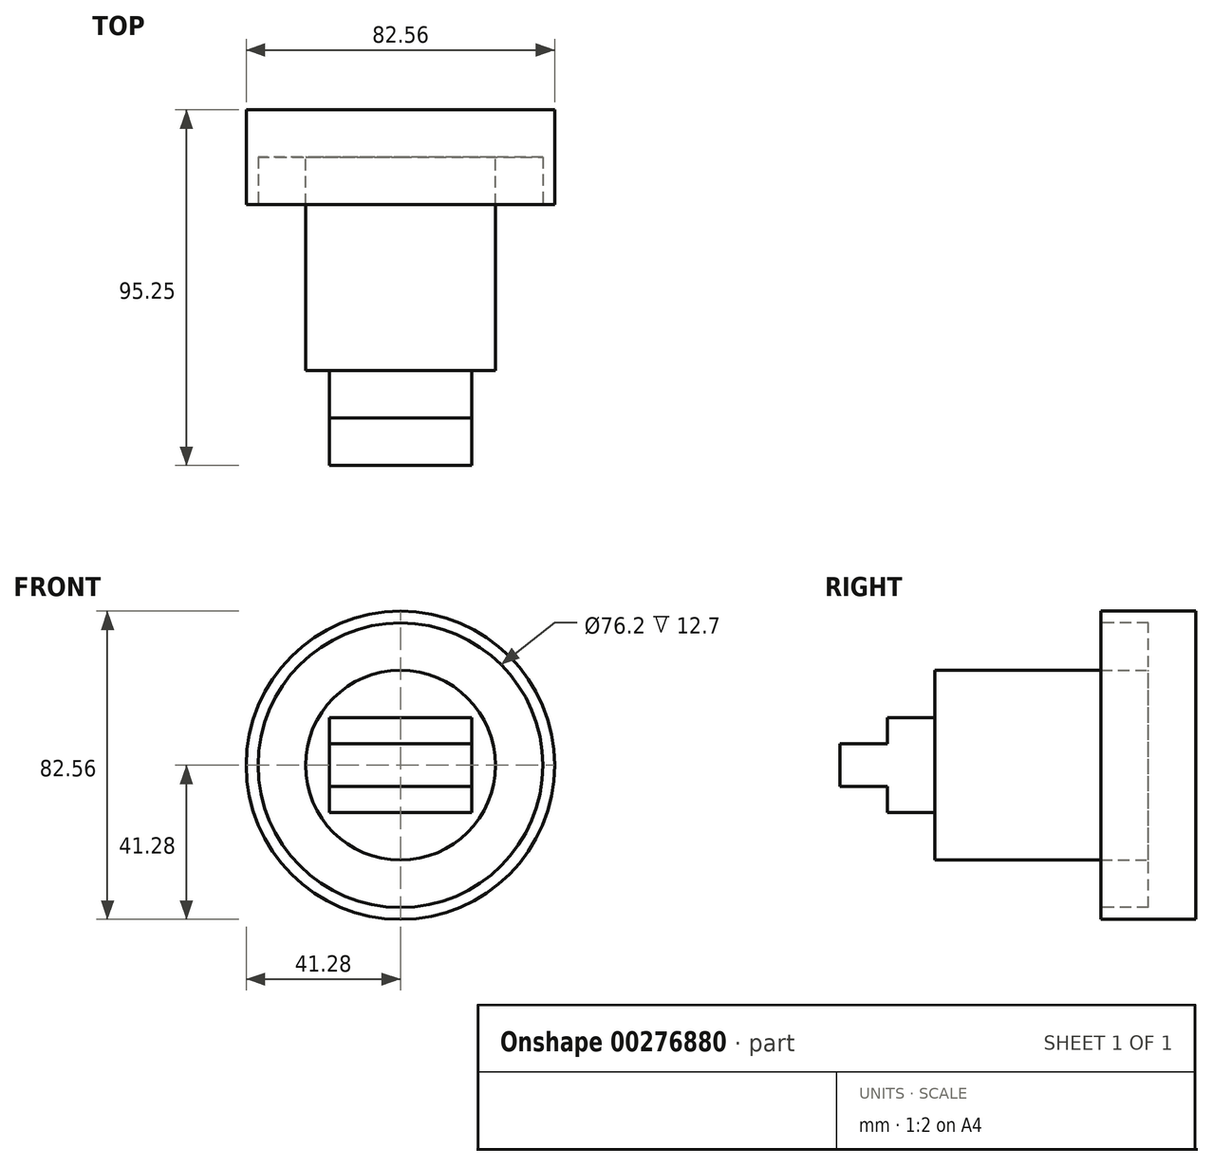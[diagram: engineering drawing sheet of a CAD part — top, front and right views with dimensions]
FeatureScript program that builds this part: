
annotation { "Feature Type Name" : "Feature", "Feature Type Description" : "" }
export const myFeature = defineFeature(function(context is Context, id is Id, definition is map)
    precondition{}
    {
        {
            var Q0;
            Q0=qCreatedBy(makeId("Front.planeOp"),FACE);
            var sketch = newSketch(context, id + "F0", { "sketchPlane" : qUnion([Q0])});
            skCircle(sketch, "E0", {"center": v(0, 0) * mm, "radius": 41.28 * mm});
            skSolve(sketch);
        }
        {
            var Q0;
            Q0 = qSketchRegion(id + "F0", true);
            extrude(context, id + "F1", {"entities" : qUnion([Q0]), "depth" : 25.4 * mm});
        }
        {
            var Q0;
            Q0=makeQuery(id+"F1.opExtrude","CAP_FACE",FACE,{"disambiguationData":[OSD([sQuery(id+"F0.wireOp",EDGE,"E0")])],"isStart":false});
            var sketch = newSketch(context, id + "F2", { "sketchPlane" : qUnion([Q0])});
            skCircle(sketch, "E1", {"center": v(0, 0) * mm, "radius": 38.1 * mm});
            skSolve(sketch);
        }
        {
            var Q0;
            Q0 = qSketchRegion(id + "F2", true);
            extrude(context, id + "F3", {"entities" : qUnion([Q0]), "operationType" : NewBodyOperationType.REMOVE, "oppositeDirection" : true, "depth" : 12.7 * mm});
        }
        {
            var Q0;
            Q0=makeQuery(id+"F3.boolean.opBoolean","COPY",FACE,{"derivedFrom":makeQuery(id+"F3.opExtrude","CAP_FACE",FACE,{"disambiguationData":[OSD([sQuery(id+"F2.wireOp",EDGE,"E1")])],"isStart":false})});
            var sketch = newSketch(context, id + "F4", { "sketchPlane" : qUnion([Q0])});
            skCircle(sketch, "E2", {"center": v(0, 0) * mm, "radius": 25.4 * mm});
            skSolve(sketch);
        }
        {
            var Q0;
            Q0 = qSketchRegion(id + "F4", true);
            extrude(context, id + "F5", {"entities" : qUnion([Q0]), "operationType" : NewBodyOperationType.ADD, "depth" : 57.15 * mm});
        }
        {
            var Q0;
            Q0=makeQuery(id+"F5.opExtrude","CAP_FACE",FACE,{"disambiguationData":[OSD([sQuery(id+"F4.wireOp",EDGE,"E2")])],"isStart":false});
            var sketch = newSketch(context, id + "F6", { "sketchPlane" : qUnion([Q0])});
            skLineSegment(sketch, "E3.bottom", {"start": v(19.05, 12.7) * mm, "end": v(-19.05, 12.7) * mm});
            skLineSegment(sketch, "E3.top", {"start": v(19.05, -12.7) * mm, "end": v(-19.05, -12.7) * mm});
            skLineSegment(sketch, "E3.left", {"start": v(19.05, 12.7) * mm, "end": v(19.05, -12.7) * mm});
            skLineSegment(sketch, "E3.right", {"start": v(-19.05, 12.7) * mm, "end": v(-19.05, -12.7) * mm});
            skPoint(sketch, "E3.middle", {"position": v(0, 0) * mm});
            skSolve(sketch);
        }
        {
            var Q0;
            Q0 = qSketchRegion(id + "F6", true);
            extrude(context, id + "F7", {"entities" : qUnion([Q0]), "operationType" : NewBodyOperationType.ADD, "depth" : 25.4 * mm});
        }
        {
            var Q0;
            Q0=makeQuery(id+"F7.opExtrude","CAP_FACE",FACE,{"disambiguationData":[OSD([sQuery(id+"F6.wireOp",EDGE,"E3.bottom"),sQuery(id+"F6.wireOp",EDGE,"E3.top"),sQuery(id+"F6.wireOp",EDGE,"E3.left"),sQuery(id+"F6.wireOp",EDGE,"E3.right")])],"isStart":false});
            var sketch = newSketch(context, id + "F8", { "sketchPlane" : qUnion([Q0])});
            skLineSegment(sketch, "E4.bottom", {"start": v(-19.05, 12.7) * mm, "end": v(19.05, 12.7) * mm});
            skLineSegment(sketch, "E4.top", {"start": v(-19.05, 5.71) * mm, "end": v(19.05, 5.71) * mm});
            skLineSegment(sketch, "E4.left", {"start": v(-19.05, 12.7) * mm, "end": v(-19.05, 5.71) * mm});
            skLineSegment(sketch, "E4.right", {"start": v(19.05, 12.7) * mm, "end": v(19.05, 5.71) * mm});
            skLineSegment(sketch, "E5.bottom", {"start": v(-19.05, -12.7) * mm, "end": v(19.05, -12.7) * mm});
            skLineSegment(sketch, "E5.top", {"start": v(-19.05, -5.71) * mm, "end": v(19.05, -5.71) * mm});
            skLineSegment(sketch, "E5.left", {"start": v(-19.05, -12.7) * mm, "end": v(-19.05, -5.71) * mm});
            skLineSegment(sketch, "E5.right", {"start": v(19.05, -12.7) * mm, "end": v(19.05, -5.71) * mm});
            skSolve(sketch);
        }
        {
            var Q0;
            Q0 = qSketchRegion(id + "F8", true);
            extrude(context, id + "F9", {"entities" : qUnion([Q0]), "operationType" : NewBodyOperationType.REMOVE, "oppositeDirection" : true, "depth" : 12.7 * mm});
        }
    });
